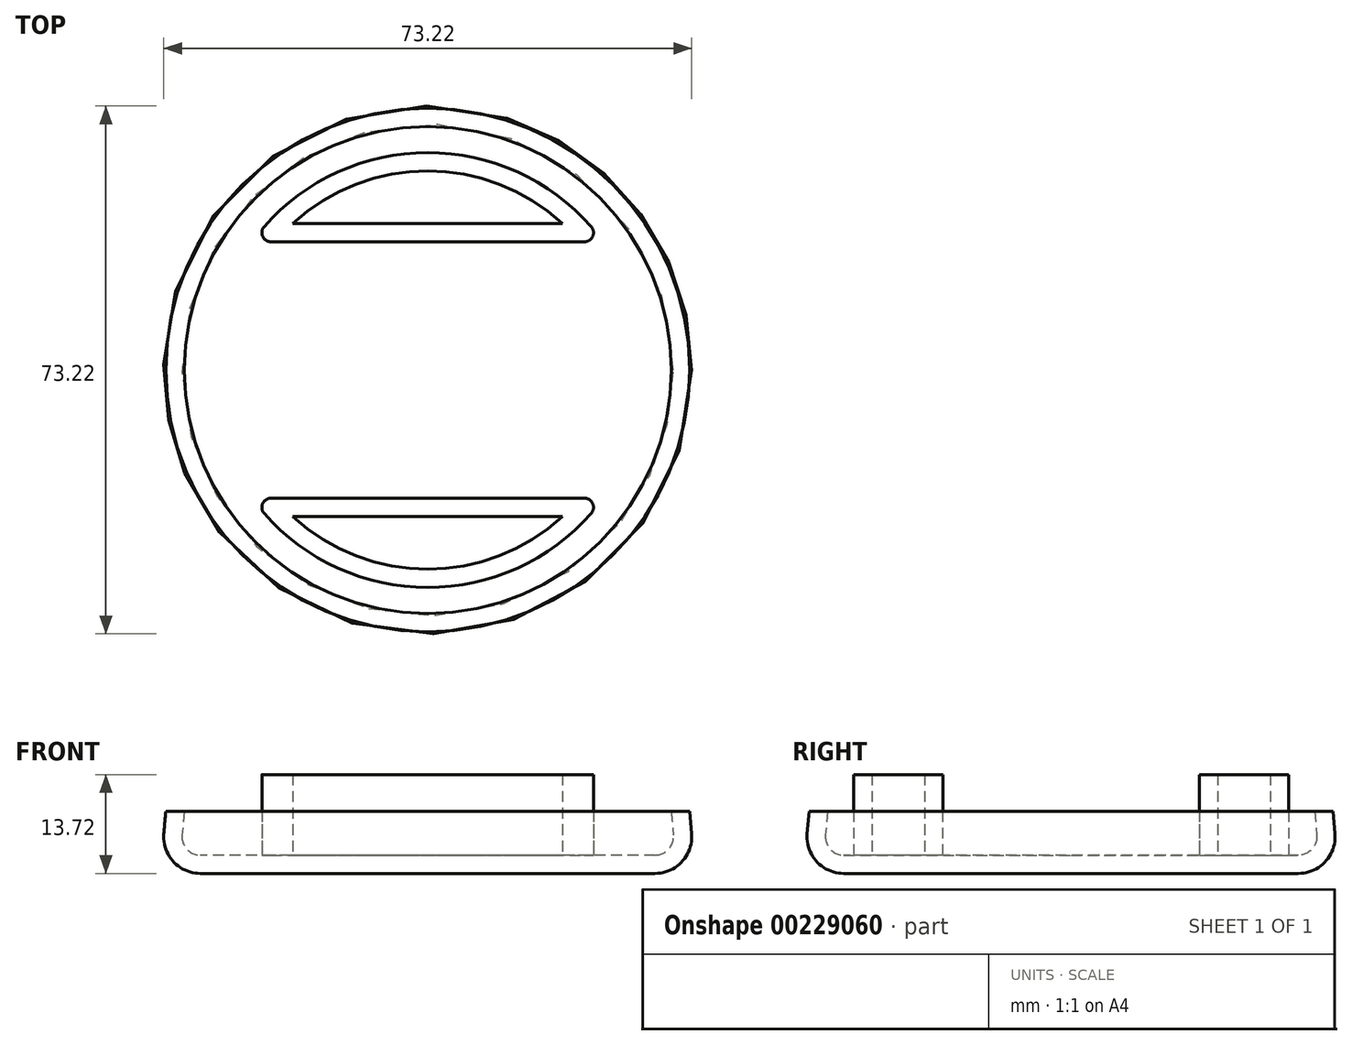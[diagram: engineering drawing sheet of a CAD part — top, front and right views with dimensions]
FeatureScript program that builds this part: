
annotation { "Feature Type Name" : "Feature", "Feature Type Description" : "" }
export const myFeature = defineFeature(function(context is Context, id is Id, definition is map)
    precondition{}
    {
        {
            var Q0;
            Q0=qCreatedBy(makeId("Top.planeOp"),FACE);
            var sketch = newSketch(context, id + "F0", { "sketchPlane" : qUnion([Q0])});
            skCircle(sketch, "E0", {"center": v(0, 0) * mm, "radius": 36.32 * mm});
            skSolve(sketch);
        }
        {
            var Q0;
            Q0 = qSketchRegion(id + "F0", true);
            extrude(context, id + "F1", {"entities" : qUnion([Q0]), "oppositeDirection" : true, "depth" : 8.64 * mm, "hasDraft" : true, "draftAngle" : 5 * degree});
        }
        {
            var Q0;
            Q0=makeQuery(id+"F1.opExtrude","CAP_FACE",FACE,{"disambiguationData":[OSD([sQuery(id+"F0.wireOp",EDGE,"E0")])],"isStart":true});
            shell(context, id + "F2", {"entities" : qUnion([Q0]), "thickness" : 2.54 * mm});
        }
        {
            var Q0;
            Q0=makeQuery(id+"F1.opExtrude","CAP_FACE",FACE,{"disambiguationData":[OSD([sQuery(id+"F0.wireOp",EDGE,"E0")])],"isStart":true});
            var sketch = newSketch(context, id + "F3", { "sketchPlane" : qUnion([Q0])});
            skArc(sketch, "E1", {"start": v(24.36, 17.78) * mm, "mid": v(0, 30.16) * mm, "end": v(-24.36, 17.78) * mm});
            skLineSegment(sketch, "E2.bottom", {"start": v(-24.36, 17.78) * mm, "end": v(24.36, 17.78) * mm});
            skLineSegment(sketch, "E2.top", {"start": v(-24.36, -17.78) * mm, "end": v(24.36, -17.78) * mm});
            skLineSegment(sketch, "E3", {"start": v(0, 17.78) * mm, "end": v(0, -17.78) * mm, "construction": true});
            skArc(sketch, "E4.trimOffspring", {"start": v(-24.36, -17.78) * mm, "mid": v(0, -30.16) * mm, "end": v(24.36, -17.78) * mm});
            skSolve(sketch);
        }
        {
            var Q0;
            Q0 = qSketchRegion(id + "F3", true);
            var Q1;
            {var subQ0=sQuery(id+"F0.wireOp",EDGE,"E0");Q1=makeQuery(id+"F2.opShell","OFFSET_FACE",FACE,{"disambiguationData":[OSD([subQ0]),TDD([makeQuery(id+"F1.opExtrude","CAP_FACE",FACE,{"disambiguationData":[OSD([subQ0])],"isStart":false})])]});}
            extrude(context, id + "F4", {"entities" : qUnion([Q0]), "operationType" : NewBodyOperationType.ADD, "depth" : 5.08 * mm, "hasSecondDirection" : true, "secondDirectionBound" : BoundingType.UP_TO_SURFACE, "secondDirectionOppositeDirection" : true, "secondDirectionBoundEntityFace" : qUnion([Q1]), "secondDirectionDepth" : 25.4 * mm});
        }
        {
            var Q0;
            {var subQ0=sQuery(id+"F3.wireOp",EDGE,"E2.bottom");var subQ1=sQuery(id+"F3.wireOp",EDGE,"E1");Q0=makeQuery(id+"F4.opExtrude","SWEPT_EDGE",EDGE,{"disambiguationData":[OSD([subQ1,subQ0]),TDD([makeQuery(id+"F3.imprint","INTERSECT",VERTEX,{"disambiguationData":[OD(1.0)],"derivedFrom":[subQ1,subQ0]})])]});}
            var Q1;
            {var subQ0=sQuery(id+"F3.wireOp",EDGE,"E2.bottom");var subQ1=sQuery(id+"F3.wireOp",EDGE,"E1");Q1=makeQuery(id+"F4.opExtrude","SWEPT_EDGE",EDGE,{"disambiguationData":[OSD([subQ1,subQ0]),TDD([makeQuery(id+"F3.imprint","INTERSECT",VERTEX,{"disambiguationData":[OD(0.0)],"derivedFrom":[subQ1,subQ0]})])]});}
            var Q2;
            {var subQ0=sQuery(id+"F3.wireOp",EDGE,"E4.trimOffspring");var subQ1=sQuery(id+"F3.wireOp",EDGE,"E2.top");Q2=makeQuery(id+"F4.opExtrude","SWEPT_EDGE",EDGE,{"disambiguationData":[OSD([subQ1,subQ0]),TDD([makeQuery(id+"F3.imprint","INTERSECT",VERTEX,{"disambiguationData":[OD(1.0)],"derivedFrom":[subQ1,subQ0]})])]});}
            var Q3;
            {var subQ0=sQuery(id+"F3.wireOp",EDGE,"E4.trimOffspring");var subQ1=sQuery(id+"F3.wireOp",EDGE,"E2.top");Q3=makeQuery(id+"F4.opExtrude","SWEPT_EDGE",EDGE,{"disambiguationData":[OSD([subQ1,subQ0]),TDD([makeQuery(id+"F3.imprint","INTERSECT",VERTEX,{"disambiguationData":[OD(0.0)],"derivedFrom":[subQ1,subQ0]})])]});}
            fillet(context, id + "F5", {"entities" : qUnion([Q0, Q1, Q2, Q3]), "radius" : 1.27 * mm, "tangentPropagation" : true, "allowEdgeOverflow" : false});
        }
        {
            var Q0;
            Q0=makeQuery(id+"F4.opExtrude","CAP_FACE",FACE,{"disambiguationData":[OSD([sQuery(id+"F3.wireOp",EDGE,"E1"),sQuery(id+"F3.wireOp",EDGE,"E2.bottom")])],"isStart":false});
            var Q1;
            Q1=makeQuery(id+"F4.opExtrude","CAP_FACE",FACE,{"disambiguationData":[OSD([sQuery(id+"F3.wireOp",EDGE,"E2.top"),sQuery(id+"F3.wireOp",EDGE,"E4.trimOffspring")])],"isStart":false});
            shell(context, id + "F6", {"entities" : qUnion([Q0, Q1]), "thickness" : 2.54 * mm});
        }
        {
            var Q0;
            Q0=makeQuery(id+"F6.opShell","OFFSET_FACE",FACE,{"disambiguationData":[OSD([sQuery(id+"F0.wireOp",EDGE,"E0")]),OD(0.0)]});
            var sketch = newSketch(context, id + "F7", { "sketchPlane" : qUnion([Q0])});
            skLineSegment(sketch, "E5", {"start": v(0, 20.32) * mm, "end": v(0, 27.62) * mm, "construction": true});
            skCircle(sketch, "E6", {"center": v(0, 23.97) * mm, "radius": 3.17 * mm});
            skSolve(sketch);
        }
        {
            var Q0;
            Q0=makeQuery(id+"F1.opExtrude","CAP_EDGE",EDGE,{"disambiguationData":[OSD([sQuery(id+"F0.wireOp",EDGE,"E0")])],"isStart":false});
            fillet(context, id + "F8", {"entities" : qUnion([Q0]), "radius" : 5.08 * mm, "tangentPropagation" : true, "allowEdgeOverflow" : false});
        }
        {
            var Q0;
            {var subQ0=sQuery(id+"F0.wireOp",EDGE,"E0");Q0=makeQuery(id+"F2.opShell","OFFSET_EDGE",EDGE,{"disambiguationData":[OSD([subQ0]),TDD([makeQuery(id+"F1.opExtrude","CAP_EDGE",EDGE,{"disambiguationData":[OSD([subQ0])],"isStart":false})])]});}
            fillet(context, id + "F9", {"entities" : qUnion([Q0]), "radius" : 2.54 * mm, "tangentPropagation" : true, "allowEdgeOverflow" : false});
        }
    });
